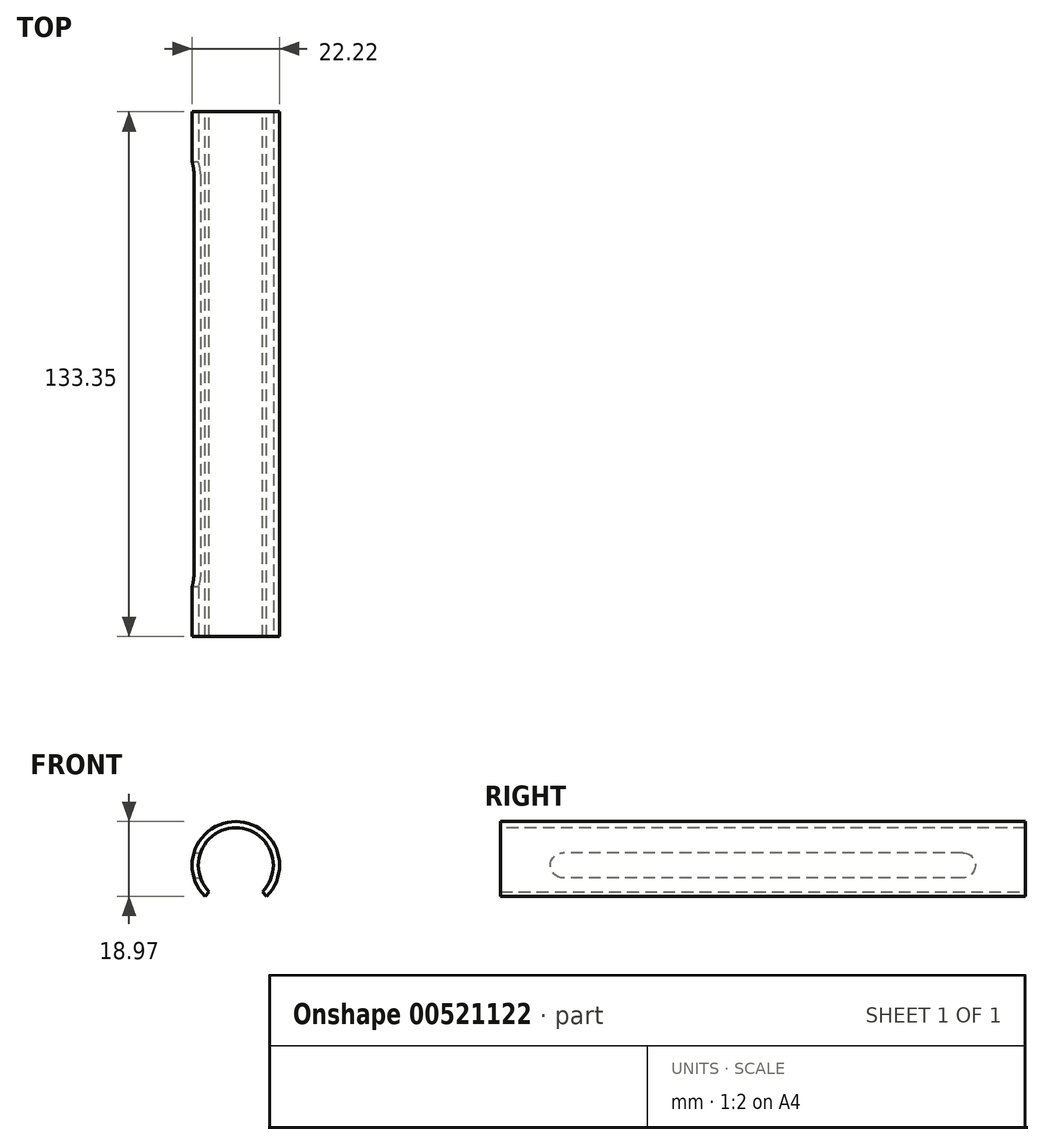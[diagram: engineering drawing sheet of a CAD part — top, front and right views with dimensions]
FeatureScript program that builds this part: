
annotation { "Feature Type Name" : "Feature", "Feature Type Description" : "" }
export const myFeature = defineFeature(function(context is Context, id is Id, definition is map)
    precondition{}
    {
        {
            var Q0;
            Q0=qCreatedBy(makeId("Right.planeOp"),FACE);
            var sketch = newSketch(context, id + "F0", { "sketchPlane" : qUnion([Q0])});
            skLineSegment(sketch, "E0", {"start": v(-6.35, 9.53) * mm, "end": v(127, 9.53) * mm});
            skLineSegment(sketch, "E1", {"start": v(-6.35, 9.53) * mm, "end": v(-6.35, 11.11) * mm});
            skLineSegment(sketch, "E2", {"start": v(-6.35, 11.11) * mm, "end": v(127, 11.11) * mm});
            skLineSegment(sketch, "E3", {"start": v(127, 9.53) * mm, "end": v(127, 11.11) * mm});
            skLineSegment(sketch, "E4", {"start": v(0, 0) * mm, "end": v(15.18, 0) * mm});
            skSolve(sketch);
        }
        {
            var Q0;
            Q0=makeQuery(id+"F0.imprint","IMPRINT",FACE,{"disambiguationData":[TD([[makeQuery(id+"F0.imprint","IMPRINT",EDGE,{"derivedFrom":sQuery(id+"F0.wireOp",EDGE,"E0")}),1.0]])]});
            var Q1;
            Q1=sQuery(id+"F0.wireOp",EDGE,"E4");
            revolve(context, id + "F1", {"entities" : qUnion([Q0]), "axis" : qUnion([Q1]), "revolveType" : RevolveType.SYMMETRIC, "angle" : 270 * degree});
        }
        {
            var Q0;
            Q0=qCreatedBy(makeId("Right.planeOp"),FACE);
            var sketch = newSketch(context, id + "F2", { "sketchPlane" : qUnion([Q0])});
            skLineSegment(sketch, "E5", {"start": v(0, 0) * mm, "end": v(6.35, 0) * mm, "construction": true});
            skArc(sketch, "E6", {"start": v(9.53, 3.17) * mm, "mid": v(6.35, 0) * mm, "end": v(9.53, -3.18) * mm});
            skLineSegment(sketch, "E7", {"start": v(9.53, 3.18) * mm, "end": v(9.53, -3.18) * mm, "construction": true});
            skLineSegment(sketch, "E8", {"start": v(9.53, -3.18) * mm, "end": v(111.12, -3.18) * mm});
            skLineSegment(sketch, "E9", {"start": v(9.53, 3.18) * mm, "end": v(111.13, 3.18) * mm});
            skLineSegment(sketch, "E10", {"start": v(111.13, 3.18) * mm, "end": v(111.13, -3.18) * mm, "construction": true});
            skArc(sketch, "E11", {"start": v(111.13, 3.18) * mm, "mid": v(114.3, 0) * mm, "end": v(111.12, -3.18) * mm});
            skSolve(sketch);
        }
        {
            var Q0;
            Q0 = qSketchRegion(id + "F2", true);
            extrude(context, id + "F3", {"entities" : qUnion([Q0]), "operationType" : NewBodyOperationType.REMOVE, "oppositeDirection" : true, "depth" : 25.4 * mm, "offsetDistance" : 25.4 * mm});
        }
    });
